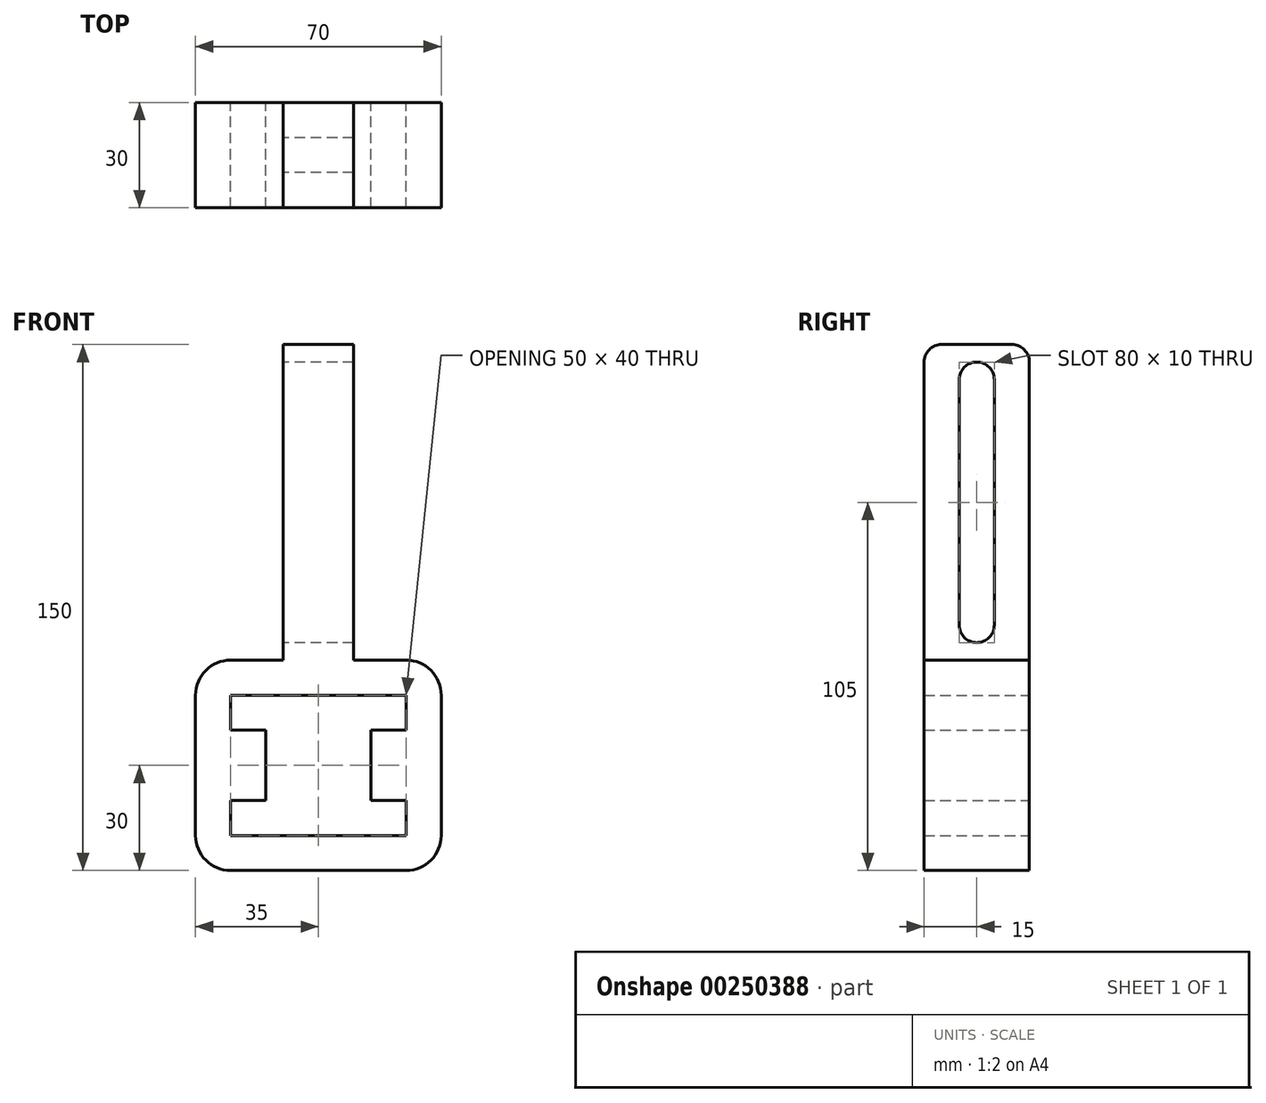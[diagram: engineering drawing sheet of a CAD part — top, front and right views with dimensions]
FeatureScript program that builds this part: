
annotation { "Feature Type Name" : "Feature", "Feature Type Description" : "" }
export const myFeature = defineFeature(function(context is Context, id is Id, definition is map)
    precondition{}
    {
        {
            var Q0;
            Q0=qCreatedBy(makeId("Front.planeOp"),FACE);
            var sketch = newSketch(context, id + "F0", { "sketchPlane" : qUnion([Q0])});
            skLineSegment(sketch, "E0.top", {"start": v(-10, -45) * mm, "end": v(10, -45) * mm});
            skPoint(sketch, "E0.middle", {"position": v(0, 0) * mm});
            skLineSegment(sketch, "E1.bottom", {"start": v(-25, -45) * mm, "end": v(25, -45) * mm});
            skLineSegment(sketch, "E1.top", {"start": v(-25, -105) * mm, "end": v(25, -105) * mm});
            skLineSegment(sketch, "E1.left", {"start": v(-35, -55) * mm, "end": v(-35, -95) * mm});
            skLineSegment(sketch, "E1.right", {"start": v(35, -55) * mm, "end": v(35, -95) * mm});
            skPoint(sketch, "E2.visualSharp", {"position": v(35, -45) * mm});
            skArc(sketch, "E2.filletArc", {"start": v(35, -55) * mm, "mid": v(32.07, -47.93) * mm, "end": v(25, -45) * mm});
            skPoint(sketch, "E3.visualSharp", {"position": v(-35, -45) * mm});
            skArc(sketch, "E3.filletArc", {"start": v(-25, -45) * mm, "mid": v(-32.07, -47.93) * mm, "end": v(-35, -55) * mm});
            skPoint(sketch, "E4.visualSharp", {"position": v(-35, -105) * mm});
            skArc(sketch, "E4.filletArc", {"start": v(-35, -95) * mm, "mid": v(-32.07, -102.07) * mm, "end": v(-25, -105) * mm});
            skPoint(sketch, "E5.visualSharp", {"position": v(35, -105) * mm});
            skArc(sketch, "E5.filletArc", {"start": v(25, -105) * mm, "mid": v(32.07, -102.07) * mm, "end": v(35, -95) * mm});
            skLineSegment(sketch, "E6", {"start": v(0, 0) * mm, "end": v(0, -111.7) * mm, "construction": true});
            skPoint(sketch, "E6.endSnap0", {"position": v(0, -105) * mm});
            skSolve(sketch);
        }
        {
            var Q0;
            Q0=makeQuery(id+"F0.imprint","IMPRINT",FACE,{"disambiguationData":[TD([[makeQuery(id+"F0.imprint","IMPRINT",EDGE,{"derivedFrom":sQuery(id+"F0.wireOp",EDGE,"E1.top")}),1.0]])]});
            extrude(context, id + "F1", {"entities" : qUnion([Q0]), "depth" : 30 * mm});
        }
        {
            var Q0;
            Q0=makeQuery(id+"F1.opExtrude","CAP_FACE",FACE,{"disambiguationData":[OSD([sQuery(id+"F0.wireOp",EDGE,"E1.bottom"),sQuery(id+"F0.wireOp",EDGE,"E1.top"),sQuery(id+"F0.wireOp",EDGE,"E1.left"),sQuery(id+"F0.wireOp",EDGE,"E1.right"),sQuery(id+"F0.wireOp",EDGE,"E2.filletArc"),sQuery(id+"F0.wireOp",EDGE,"E3.filletArc"),sQuery(id+"F0.wireOp",EDGE,"E4.filletArc"),sQuery(id+"F0.wireOp",EDGE,"E5.filletArc")])],"isStart":false});
            var sketch = newSketch(context, id + "F2", { "sketchPlane" : qUnion([Q0])});
            skLineSegment(sketch, "E7", {"start": v(-25, -55) * mm, "end": v(25, -55) * mm});
            skLineSegment(sketch, "E8", {"start": v(25, -55) * mm, "end": v(25, -65) * mm});
            skLineSegment(sketch, "E9", {"start": v(25, -65) * mm, "end": v(15, -65) * mm});
            skLineSegment(sketch, "E10", {"start": v(15, -65) * mm, "end": v(15, -85) * mm});
            skLineSegment(sketch, "E11", {"start": v(15, -85) * mm, "end": v(25, -85) * mm});
            skLineSegment(sketch, "E12", {"start": v(25, -85) * mm, "end": v(25, -95) * mm});
            skLineSegment(sketch, "E13", {"start": v(25, -95) * mm, "end": v(-25, -95) * mm});
            skLineSegment(sketch, "E14", {"start": v(-25, -95) * mm, "end": v(-25, -85) * mm});
            skLineSegment(sketch, "E15", {"start": v(-25, -85) * mm, "end": v(-15, -85) * mm});
            skLineSegment(sketch, "E16", {"start": v(-15, -85) * mm, "end": v(-15, -65) * mm});
            skLineSegment(sketch, "E17", {"start": v(-15, -65) * mm, "end": v(-25, -65) * mm});
            skLineSegment(sketch, "E18", {"start": v(-25, -65) * mm, "end": v(-25, -55) * mm});
            skSolve(sketch);
        }
        {
            var Q0;
            Q0=makeQuery(id+"F2.imprint","IMPRINT",FACE,{"disambiguationData":[TD([[makeQuery(id+"F2.imprint","IMPRINT",EDGE,{"derivedFrom":sQuery(id+"F2.wireOp",EDGE,"E7")}),-1.0]])]});
            extrude(context, id + "F3", {"entities" : qUnion([Q0]), "depth" : 25 * mm, "hasSecondDirection" : true, "secondDirectionOppositeDirection" : true, "secondDirectionDepth" : 40 * mm});
        }
        {
            var Q0;
            Q0=makeQuery(id+"F3.opExtrude","SWEPT_BODY",BODY,{"disambiguationData":[OSD([sQuery(id+"F2.wireOp",EDGE,"E7"),sQuery(id+"F2.wireOp",EDGE,"E8"),sQuery(id+"F2.wireOp",EDGE,"E9"),sQuery(id+"F2.wireOp",EDGE,"E10"),sQuery(id+"F2.wireOp",EDGE,"E11"),sQuery(id+"F2.wireOp",EDGE,"E12"),sQuery(id+"F2.wireOp",EDGE,"E13"),sQuery(id+"F2.wireOp",EDGE,"E14"),sQuery(id+"F2.wireOp",EDGE,"E15"),sQuery(id+"F2.wireOp",EDGE,"E16"),sQuery(id+"F2.wireOp",EDGE,"E17"),sQuery(id+"F2.wireOp",EDGE,"E18")])]});
            var Q1;
            Q1=makeQuery(id+"F1.opExtrude","SWEPT_BODY",BODY,{"disambiguationData":[OSD([sQuery(id+"F0.wireOp",EDGE,"E1.bottom"),sQuery(id+"F0.wireOp",EDGE,"E1.top"),sQuery(id+"F0.wireOp",EDGE,"E1.left"),sQuery(id+"F0.wireOp",EDGE,"E1.right"),sQuery(id+"F0.wireOp",EDGE,"E2.filletArc"),sQuery(id+"F0.wireOp",EDGE,"E3.filletArc"),sQuery(id+"F0.wireOp",EDGE,"E4.filletArc"),sQuery(id+"F0.wireOp",EDGE,"E5.filletArc")])]});
            booleanBodies(context, id + "F4", {"operationType" : BooleanOperationType.SUBTRACTION, "tools" : qUnion([Q0]), "targets" : qUnion([Q1])});
        }
        {
            var Q0;
            Q0=makeQuery(id+"F1.opExtrude","SWEPT_FACE",FACE,{"disambiguationData":[OSD([sQuery(id+"F0.wireOp",EDGE,"E1.bottom")])]});
            var sketch = newSketch(context, id + "F5", { "sketchPlane" : qUnion([Q0])});
            skLineSegment(sketch, "E19.bottom", {"start": v(-10, 0) * mm, "end": v(10, 0) * mm});
            skLineSegment(sketch, "E19.top", {"start": v(-10, -30) * mm, "end": v(10, -30) * mm});
            skLineSegment(sketch, "E19.left", {"start": v(-10, 0) * mm, "end": v(-10, -30) * mm});
            skLineSegment(sketch, "E19.right", {"start": v(10, 0) * mm, "end": v(10, -30) * mm});
            skSolve(sketch);
        }
        {
            var Q0;
            Q0=makeQuery(id+"F5.imprint","IMPRINT",FACE,{"disambiguationData":[TD([[makeQuery(id+"F5.imprint","IMPRINT",EDGE,{"derivedFrom":sQuery(id+"F5.wireOp",EDGE,"E19.bottom")}),-1.0]])]});
            extrude(context, id + "F6", {"entities" : qUnion([Q0]), "operationType" : NewBodyOperationType.ADD, "depth" : 90 * mm});
        }
        {
            var Q0;
            Q0=makeQuery(id+"F6.opExtrude","CAP_EDGE",EDGE,{"disambiguationData":[OSD([sQuery(id+"F5.wireOp",EDGE,"E19.top")])],"isStart":false});
            var Q1;
            Q1=makeQuery(id+"F6.opExtrude","CAP_EDGE",EDGE,{"disambiguationData":[OSD([sQuery(id+"F5.wireOp",EDGE,"E19.bottom")])],"isStart":false});
            fillet(context, id + "F7", {"entities" : qUnion([Q0, Q1]), "radius" : 5 * mm, "tangentPropagation" : true, "allowEdgeOverflow" : false});
        }
        {
            var Q0;
            Q0=makeQuery(id+"F6.opExtrude","SWEPT_FACE",FACE,{"disambiguationData":[OSD([sQuery(id+"F5.wireOp",EDGE,"E19.right")])]});
            var sketch = newSketch(context, id + "F8", { "sketchPlane" : qUnion([Q0])});
            skArc(sketch, "E20", {"start": v(-10, 35) * mm, "mid": v(-15, 40) * mm, "end": v(-20, 35) * mm});
            skArc(sketch, "E21", {"start": v(-20, -35) * mm, "mid": v(-15, -40) * mm, "end": v(-10, -35) * mm});
            skLineSegment(sketch, "E22", {"start": v(-15, 35) * mm, "end": v(-37.17, 35) * mm, "construction": true});
            skLineSegment(sketch, "E23", {"start": v(-15, -35) * mm, "end": v(-48.23, -35) * mm, "construction": true});
            skLineSegment(sketch, "E24", {"start": v(-20, 35) * mm, "end": v(-20, -35) * mm});
            skLineSegment(sketch, "E25.MirrorCS", {"start": v(-10, 35) * mm, "end": v(-10, -35) * mm});
            skSolve(sketch);
        }
        {
            var Q0;
            Q0=makeQuery(id+"F8.imprint","IMPRINT",FACE,{"disambiguationData":[TD([[makeQuery(id+"F8.imprint","IMPRINT",EDGE,{"derivedFrom":sQuery(id+"F8.wireOp",EDGE,"E20")}),1.0]])]});
            extrude(context, id + "F9", {"entities" : qUnion([Q0]), "depth" : 25 * mm, "hasSecondDirection" : true, "secondDirectionOppositeDirection" : true, "secondDirectionDepth" : 40 * mm});
        }
        {
            var Q0;
            Q0=makeQuery(id+"F9.opExtrude","SWEPT_BODY",BODY,{"disambiguationData":[OSD([sQuery(id+"F8.wireOp",EDGE,"E20"),sQuery(id+"F8.wireOp",EDGE,"E21"),sQuery(id+"F8.wireOp",EDGE,"E24"),sQuery(id+"F8.wireOp",EDGE,"E25.MirrorCS")])]});
            var Q1;
            Q1=makeQuery(id+"F1.opExtrude","SWEPT_BODY",BODY,{"disambiguationData":[OSD([sQuery(id+"F0.wireOp",EDGE,"E1.bottom"),sQuery(id+"F0.wireOp",EDGE,"E1.top"),sQuery(id+"F0.wireOp",EDGE,"E1.left"),sQuery(id+"F0.wireOp",EDGE,"E1.right"),sQuery(id+"F0.wireOp",EDGE,"E2.filletArc"),sQuery(id+"F0.wireOp",EDGE,"E3.filletArc"),sQuery(id+"F0.wireOp",EDGE,"E4.filletArc"),sQuery(id+"F0.wireOp",EDGE,"E5.filletArc")])]});
            booleanBodies(context, id + "F10", {"operationType" : BooleanOperationType.SUBTRACTION, "tools" : qUnion([Q0]), "targets" : qUnion([Q1])});
        }
    });
